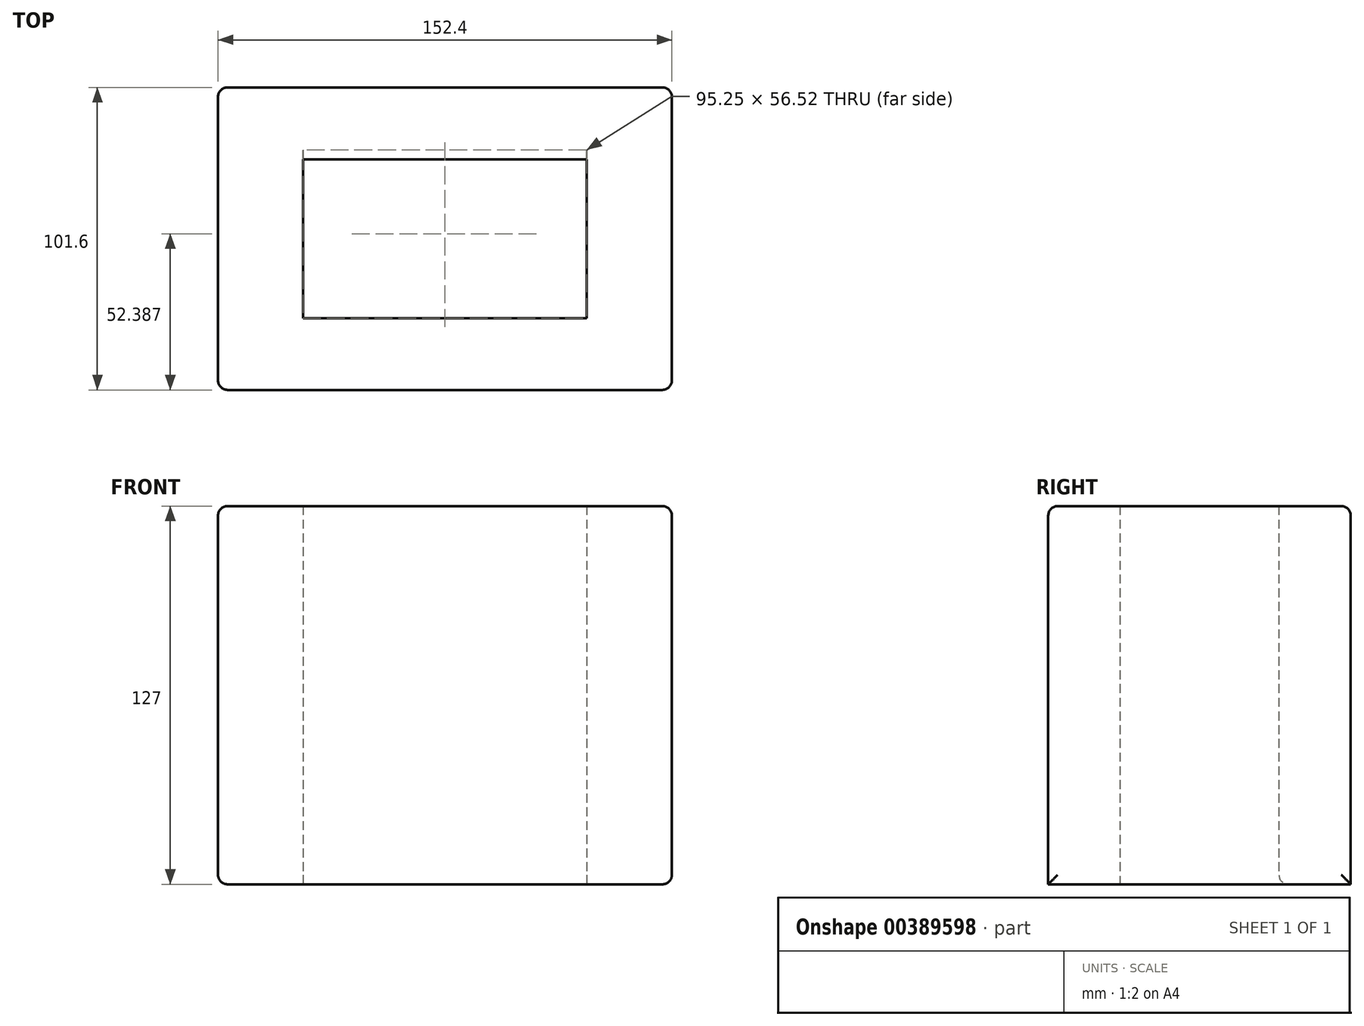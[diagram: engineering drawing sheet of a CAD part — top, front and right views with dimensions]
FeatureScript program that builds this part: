
annotation { "Feature Type Name" : "Feature", "Feature Type Description" : "" }
export const myFeature = defineFeature(function(context is Context, id is Id, definition is map)
    precondition{}
    {
        {
            var Q0;
            Q0=qCreatedBy(makeId("Top.planeOp"),FACE);
            var sketch = newSketch(context, id + "F0", { "sketchPlane" : qUnion([Q0])});
            skLineSegment(sketch, "E0.bottom", {"start": v(-76.2, 50.8) * mm, "end": v(76.2, 50.8) * mm});
            skLineSegment(sketch, "E0.top", {"start": v(-76.2, -50.8) * mm, "end": v(76.2, -50.8) * mm});
            skLineSegment(sketch, "E0.left", {"start": v(-76.2, 50.8) * mm, "end": v(-76.2, -50.8) * mm});
            skLineSegment(sketch, "E0.right", {"start": v(76.2, 50.8) * mm, "end": v(76.2, -50.8) * mm});
            skPoint(sketch, "E0.middle", {"position": v(0, 0) * mm});
            skLineSegment(sketch, "E1.bottom", {"start": v(-47.63, 26.67) * mm, "end": v(47.63, 26.67) * mm});
            skLineSegment(sketch, "E1.top", {"start": v(-47.63, -26.67) * mm, "end": v(47.62, -26.67) * mm});
            skLineSegment(sketch, "E1.left", {"start": v(-47.63, 26.67) * mm, "end": v(-47.63, -26.67) * mm});
            skLineSegment(sketch, "E1.right", {"start": v(47.63, 26.67) * mm, "end": v(47.62, -26.67) * mm});
            skSolve(sketch);
        }
        {
            var Q0;
            Q0 = qSketchRegion(id + "F0", true);
            extrude(context, id + "F1", {"entities" : qUnion([Q0]), "depth" : 127 * mm});
        }
        {
            var Q0;
            Q0=makeQuery(id+"F1.opExtrude","CAP_EDGE",EDGE,{"disambiguationData":[OSD([sQuery(id+"F0.wireOp",EDGE,"E0.bottom")])],"isStart":false});
            var Q1;
            Q1=makeQuery(id+"F1.opExtrude","CAP_EDGE",EDGE,{"disambiguationData":[OSD([sQuery(id+"F0.wireOp",EDGE,"E0.top")])],"isStart":false});
            var Q2;
            Q2=makeQuery(id+"F1.opExtrude","CAP_EDGE",EDGE,{"disambiguationData":[OSD([sQuery(id+"F0.wireOp",EDGE,"E0.left")])],"isStart":false});
            var Q3;
            Q3=makeQuery(id+"F1.opExtrude","CAP_EDGE",EDGE,{"disambiguationData":[OSD([sQuery(id+"F0.wireOp",EDGE,"E0.right")])],"isStart":false});
            var Q4;
            Q4=makeQuery(id+"F1.opExtrude","SWEPT_EDGE",EDGE,{"disambiguationData":[OSD([sQuery(id+"F0.wireOp",EDGE,"E0.bottom"),sQuery(id+"F0.wireOp",EDGE,"E0.right")])]});
            var Q5;
            Q5=makeQuery(id+"F1.opExtrude","SWEPT_EDGE",EDGE,{"disambiguationData":[OSD([sQuery(id+"F0.wireOp",EDGE,"E0.top"),sQuery(id+"F0.wireOp",EDGE,"E0.right")])]});
            var Q6;
            Q6=makeQuery(id+"F1.opExtrude","SWEPT_EDGE",EDGE,{"disambiguationData":[OSD([sQuery(id+"F0.wireOp",EDGE,"E0.top"),sQuery(id+"F0.wireOp",EDGE,"E0.left")])]});
            var Q7;
            Q7=makeQuery(id+"F1.opExtrude","SWEPT_EDGE",EDGE,{"disambiguationData":[OSD([sQuery(id+"F0.wireOp",EDGE,"E0.bottom"),sQuery(id+"F0.wireOp",EDGE,"E0.left")])]});
            var Q8;
            Q8=makeQuery(id+"F1.opExtrude","CAP_EDGE",EDGE,{"disambiguationData":[OSD([sQuery(id+"F0.wireOp",EDGE,"E1.bottom")])],"isStart":true});
            var Q9;
            Q9=makeQuery(id+"F1.opExtrude","SWEPT_FACE",FACE,{"disambiguationData":[OSD([sQuery(id+"F0.wireOp",EDGE,"E0.right")])]});
            var Q10;
            Q10=makeQuery(id+"F1.opExtrude","CAP_EDGE",EDGE,{"disambiguationData":[OSD([sQuery(id+"F0.wireOp",EDGE,"E0.left")])],"isStart":true});
            fillet(context, id + "F2", {"entities" : qUnion([Q0, Q1, Q2, Q3, Q4, Q5, Q6, Q7, Q8, Q9, Q10]), "radius" : 3.17 * mm, "tangentPropagation" : true, "allowEdgeOverflow" : false});
        }
    });
